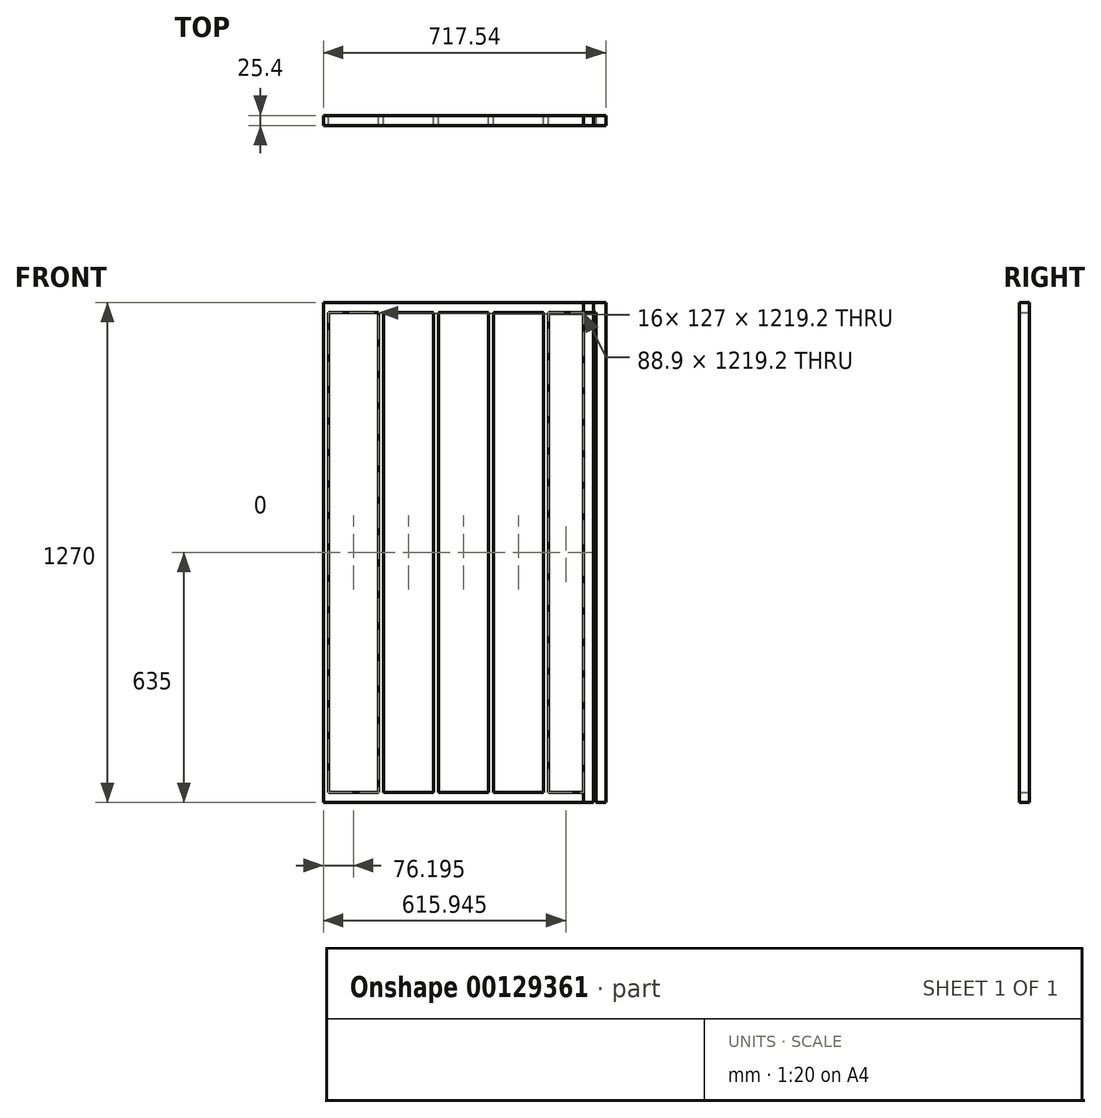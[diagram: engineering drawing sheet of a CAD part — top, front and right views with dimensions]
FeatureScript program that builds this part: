
annotation { "Feature Type Name" : "Feature", "Feature Type Description" : "" }
export const myFeature = defineFeature(function(context is Context, id is Id, definition is map)
    precondition{}
    {
        {
            var Q0;
            Q0=qCreatedBy(makeId("Front.planeOp"),FACE);
            var sketch = newSketch(context, id + "F0", { "sketchPlane" : qUnion([Q0])});
            skLineSegment(sketch, "E0", {"start": v(-930.27, 1244.6) * mm, "end": v(930.27, 1244.6) * mm});
            skLineSegment(sketch, "E1", {"start": v(-930.27, 25.4) * mm, "end": v(930.27, 25.4) * mm});
            skLineSegment(sketch, "E2", {"start": v(-625.48, 25.4) * mm, "end": v(-625.48, 1244.6) * mm, "construction": true});
            skLineSegment(sketch, "E3", {"start": v(-485.77, 1244.6) * mm, "end": v(-485.77, 25.4) * mm, "construction": true});
            skLineSegment(sketch, "E4", {"start": v(-346.08, 25.4) * mm, "end": v(-346.08, 1244.6) * mm, "construction": true});
            skLineSegment(sketch, "E5", {"start": v(-206.37, 1244.6) * mm, "end": v(-206.37, 25.4) * mm, "construction": true});
            skLineSegment(sketch, "E6", {"start": v(-66.67, 25.4) * mm, "end": v(-66.67, 1244.6) * mm, "construction": true});
            skLineSegment(sketch, "E7", {"start": v(73.03, 1244.6) * mm, "end": v(73.03, 25.4) * mm, "construction": true});
            skLineSegment(sketch, "E8", {"start": v(212.73, 25.4) * mm, "end": v(212.73, 1244.6) * mm, "construction": true});
            skLineSegment(sketch, "E9", {"start": v(352.43, 1244.6) * mm, "end": v(352.43, 25.4) * mm, "construction": true});
            skLineSegment(sketch, "E10", {"start": v(492.13, 25.4) * mm, "end": v(492.13, 1244.6) * mm, "construction": true});
            skLineSegment(sketch, "E11", {"start": v(631.82, 1244.6) * mm, "end": v(631.82, 25.4) * mm, "construction": true});
            skLineSegment(sketch, "E12.0", {"start": v(-619.12, 25.4) * mm, "end": v(-619.12, 1244.6) * mm});
            skLineSegment(sketch, "E13.0", {"start": v(-492.12, 1244.6) * mm, "end": v(-492.12, 25.4) * mm});
            skLineSegment(sketch, "E14.0", {"start": v(-479.42, 1244.6) * mm, "end": v(-479.42, 25.4) * mm});
            skLineSegment(sketch, "E15.0", {"start": v(-339.73, 25.4) * mm, "end": v(-339.73, 1244.6) * mm});
            skLineSegment(sketch, "E16.0", {"start": v(-352.43, 25.4) * mm, "end": v(-352.43, 1244.6) * mm});
            skLineSegment(sketch, "E17.0", {"start": v(-212.72, 1244.6) * mm, "end": v(-212.72, 25.4) * mm});
            skLineSegment(sketch, "E18.0", {"start": v(-200.02, 1244.6) * mm, "end": v(-200.02, 25.4) * mm});
            skLineSegment(sketch, "E19.0", {"start": v(-60.32, 25.4) * mm, "end": v(-60.32, 1244.6) * mm});
            skLineSegment(sketch, "E20.0", {"start": v(-73.02, 25.4) * mm, "end": v(-73.02, 1244.6) * mm});
            skLineSegment(sketch, "E21.0", {"start": v(66.68, 1244.6) * mm, "end": v(66.68, 25.4) * mm});
            skLineSegment(sketch, "E22.0", {"start": v(79.38, 1244.6) * mm, "end": v(79.38, 25.4) * mm});
            skLineSegment(sketch, "E23.0", {"start": v(219.08, 25.4) * mm, "end": v(219.08, 1244.6) * mm});
            skLineSegment(sketch, "E24.0", {"start": v(206.38, 25.4) * mm, "end": v(206.38, 1244.6) * mm});
            skLineSegment(sketch, "E25.0", {"start": v(346.08, 1244.6) * mm, "end": v(346.08, 25.4) * mm});
            skLineSegment(sketch, "E26.0", {"start": v(358.78, 1244.6) * mm, "end": v(358.78, 25.4) * mm});
            skLineSegment(sketch, "E27.0", {"start": v(498.48, 25.4) * mm, "end": v(498.48, 1244.6) * mm});
            skLineSegment(sketch, "E28.0", {"start": v(485.78, 25.4) * mm, "end": v(485.78, 1244.6) * mm});
            skLineSegment(sketch, "E29.0", {"start": v(625.48, 1244.6) * mm, "end": v(625.48, 25.4) * mm});
            skLineSegment(sketch, "E30.0", {"start": v(638.18, 1244.6) * mm, "end": v(638.18, 25.4) * mm});
            skLineSegment(sketch, "E31.0", {"start": v(-631.82, 25.4) * mm, "end": v(-631.82, 1244.6) * mm});
            skLineSegment(sketch, "E32.0", {"start": v(-930.27, 1270) * mm, "end": v(930.27, 1270) * mm});
            skLineSegment(sketch, "E33.0", {"start": v(-930.27, 0) * mm, "end": v(930.27, 0) * mm});
            skLineSegment(sketch, "E34", {"start": v(-765.17, 1244.6) * mm, "end": v(-765.17, 25.4) * mm, "construction": true});
            skLineSegment(sketch, "E35", {"start": v(771.52, 25.4) * mm, "end": v(771.52, 1244.6) * mm, "construction": true});
            skLineSegment(sketch, "E36.0", {"start": v(777.88, 25.4) * mm, "end": v(777.88, 1244.6) * mm});
            skLineSegment(sketch, "E37.0", {"start": v(765.18, 25.4) * mm, "end": v(765.18, 1244.6) * mm});
            skLineSegment(sketch, "E38.0", {"start": v(-771.52, 1244.6) * mm, "end": v(-771.52, 25.4) * mm});
            skLineSegment(sketch, "E39.0", {"start": v(-758.82, 1244.6) * mm, "end": v(-758.82, 25.4) * mm});
            skLineSegment(sketch, "E40", {"start": v(930.28, 25.4) * mm, "end": v(930.28, 0) * mm});
            skLineSegment(sketch, "E41", {"start": v(-930.27, 25.4) * mm, "end": v(-930.27, 0) * mm});
            skLineSegment(sketch, "E42", {"start": v(-930.27, 1270) * mm, "end": v(-930.27, 1244.6) * mm});
            skLineSegment(sketch, "E43", {"start": v(930.28, 1270) * mm, "end": v(930.28, 1244.6) * mm});
            skLineSegment(sketch, "E44", {"start": v(-190.5, 1258.47) * mm, "end": v(190.5, 1258.47) * mm});
            skLineSegment(sketch, "E45", {"start": v(0, 1258.47) * mm, "end": v(0, 1270) * mm, "construction": true});
            skLineSegment(sketch, "E46", {"start": v(-190.5, 1258.47) * mm, "end": v(-930.27, 1258.47) * mm, "construction": true});
            skLineSegment(sketch, "E47", {"start": v(190.5, 1258.47) * mm, "end": v(930.27, 1258.47) * mm, "construction": true});
            skLineSegment(sketch, "E48", {"start": v(930.28, 1258.47) * mm, "end": v(930.28, 1270) * mm, "construction": true});
            skLineSegment(sketch, "E49", {"start": v(-930.27, 1258.47) * mm, "end": v(-930.27, 1270) * mm, "construction": true});
            skLineSegment(sketch, "E50", {"start": v(-854.07, 25.4) * mm, "end": v(-854.07, 1244.6) * mm, "construction": true});
            skLineSegment(sketch, "E51", {"start": v(860.42, 25.4) * mm, "end": v(860.43, 1244.6) * mm, "construction": true});
            skLineSegment(sketch, "E52", {"start": v(-854.07, 25.4) * mm, "end": v(-854.07, -210.06) * mm, "construction": true});
            skLineSegment(sketch, "E53", {"start": v(-854.07, -210.06) * mm, "end": v(860.42, -210.06) * mm, "construction": true});
            skLineSegment(sketch, "E54", {"start": v(860.42, -210.06) * mm, "end": v(860.42, 25.4) * mm, "construction": true});
            skSolve(sketch);
        }
        {
            var Q0;
            Q0 = qSketchRegion(id + "F0", true);
            var Q1;
            {var subQ0=sQuery(id+"F0.wireOp",EDGE,"E12.0");Q1=makeQuery(id+"F0.imprint","IMPRINT",FACE,{"disambiguationData":[TD([[makeQuery(id+"F0.imprint","IMPRINT",EDGE,{"derivedFrom":subQ0}),1.0]])]});}
            var Q2;
            {var subQ0=sQuery(id+"F0.wireOp",EDGE,"E13.0");Q2=makeQuery(id+"F0.imprint","IMPRINT",FACE,{"disambiguationData":[TD([[makeQuery(id+"F0.imprint","IMPRINT",EDGE,{"derivedFrom":subQ0}),1.0]])]});}
            var Q3;
            {var subQ0=sQuery(id+"F0.wireOp",EDGE,"E15.0");Q3=makeQuery(id+"F0.imprint","IMPRINT",FACE,{"disambiguationData":[TD([[makeQuery(id+"F0.imprint","IMPRINT",EDGE,{"derivedFrom":subQ0}),1.0]])]});}
            var Q4;
            {var subQ0=sQuery(id+"F0.wireOp",EDGE,"E17.0");Q4=makeQuery(id+"F0.imprint","IMPRINT",FACE,{"disambiguationData":[TD([[makeQuery(id+"F0.imprint","IMPRINT",EDGE,{"derivedFrom":subQ0}),1.0]])]});}
            var Q5;
            {var subQ0=sQuery(id+"F0.wireOp",EDGE,"E19.0");Q5=makeQuery(id+"F0.imprint","IMPRINT",FACE,{"disambiguationData":[TD([[makeQuery(id+"F0.imprint","IMPRINT",EDGE,{"derivedFrom":subQ0}),1.0]])]});}
            var Q6;
            {var subQ0=sQuery(id+"F0.wireOp",EDGE,"E21.0");Q6=makeQuery(id+"F0.imprint","IMPRINT",FACE,{"disambiguationData":[TD([[makeQuery(id+"F0.imprint","IMPRINT",EDGE,{"derivedFrom":subQ0}),1.0]])]});}
            var Q7;
            {var subQ0=sQuery(id+"F0.wireOp",EDGE,"E23.0");Q7=makeQuery(id+"F0.imprint","IMPRINT",FACE,{"disambiguationData":[TD([[makeQuery(id+"F0.imprint","IMPRINT",EDGE,{"derivedFrom":subQ0}),1.0]])]});}
            var Q8;
            {var subQ0=sQuery(id+"F0.wireOp",EDGE,"E25.0");Q8=makeQuery(id+"F0.imprint","IMPRINT",FACE,{"disambiguationData":[TD([[makeQuery(id+"F0.imprint","IMPRINT",EDGE,{"derivedFrom":subQ0}),1.0]])]});}
            var Q9;
            {var subQ0=sQuery(id+"F0.wireOp",EDGE,"E27.0");Q9=makeQuery(id+"F0.imprint","IMPRINT",FACE,{"disambiguationData":[TD([[makeQuery(id+"F0.imprint","IMPRINT",EDGE,{"derivedFrom":subQ0}),1.0]])]});}
            var Q10;
            {var subQ0=sQuery(id+"F0.wireOp",EDGE,"E29.0");Q10=makeQuery(id+"F0.imprint","IMPRINT",FACE,{"disambiguationData":[TD([[makeQuery(id+"F0.imprint","IMPRINT",EDGE,{"derivedFrom":subQ0}),1.0]])]});}
            extrude(context, id + "F1", {"entities" : qUnion([Q0, Q1, Q2, Q3, Q4, Q5, Q6, Q7, Q8, Q9, Q10]), "depth" : 25.4 * mm});
        }
        {
            var Q0;
            Q0=makeQuery(id+"F1.opExtrude","CAP_FACE",FACE,{"disambiguationData":[OSD([sQuery(id+"F0.wireOp",EDGE,"E0"),sQuery(id+"F0.wireOp",EDGE,"E1"),sQuery(id+"F0.wireOp",EDGE,"E12.0"),sQuery(id+"F0.wireOp",EDGE,"E13.0"),sQuery(id+"F0.wireOp",EDGE,"E14.0"),sQuery(id+"F0.wireOp",EDGE,"E15.0"),sQuery(id+"F0.wireOp",EDGE,"E16.0"),sQuery(id+"F0.wireOp",EDGE,"E17.0"),sQuery(id+"F0.wireOp",EDGE,"E18.0"),sQuery(id+"F0.wireOp",EDGE,"E19.0"),sQuery(id+"F0.wireOp",EDGE,"E20.0"),sQuery(id+"F0.wireOp",EDGE,"E21.0"),sQuery(id+"F0.wireOp",EDGE,"E22.0"),sQuery(id+"F0.wireOp",EDGE,"E23.0"),sQuery(id+"F0.wireOp",EDGE,"E24.0"),sQuery(id+"F0.wireOp",EDGE,"E25.0"),sQuery(id+"F0.wireOp",EDGE,"E26.0"),sQuery(id+"F0.wireOp",EDGE,"E27.0"),sQuery(id+"F0.wireOp",EDGE,"E28.0"),sQuery(id+"F0.wireOp",EDGE,"E29.0"),sQuery(id+"F0.wireOp",EDGE,"E30.0"),sQuery(id+"F0.wireOp",EDGE,"E31.0"),sQuery(id+"F0.wireOp",EDGE,"E32.0"),sQuery(id+"F0.wireOp",EDGE,"E33.0"),sQuery(id+"F0.wireOp",EDGE,"E36.0"),sQuery(id+"F0.wireOp",EDGE,"E37.0"),sQuery(id+"F0.wireOp",EDGE,"E38.0"),sQuery(id+"F0.wireOp",EDGE,"E39.0"),sQuery(id+"F0.wireOp",EDGE,"E40"),sQuery(id+"F0.wireOp",EDGE,"E41"),sQuery(id+"F0.wireOp",EDGE,"E42"),sQuery(id+"F0.wireOp",EDGE,"E43")])],"isStart":false});
            var sketch = newSketch(context, id + "F2", { "sketchPlane" : qUnion([Q0])});
            skLineSegment(sketch, "E55.bottom", {"start": v(-200.03, 1292.02) * mm, "end": v(206.37, 1292.02) * mm});
            skLineSegment(sketch, "E55.top", {"start": v(-200.02, -104.94) * mm, "end": v(206.38, -104.94) * mm});
            skLineSegment(sketch, "E55.left", {"start": v(-200.03, 1292.02) * mm, "end": v(-200.02, -104.94) * mm});
            skLineSegment(sketch, "E55.right", {"start": v(206.37, 1292.02) * mm, "end": v(206.38, -104.94) * mm});
            skLineSegment(sketch, "E56.bottom", {"start": v(-930.27, 1270) * mm, "end": v(-860.42, 1270) * mm});
            skLineSegment(sketch, "E56.top", {"start": v(-930.27, 0) * mm, "end": v(-860.42, 0) * mm});
            skLineSegment(sketch, "E56.left", {"start": v(-930.27, 1270) * mm, "end": v(-930.27, 0) * mm});
            skLineSegment(sketch, "E56.right", {"start": v(-860.42, 1270) * mm, "end": v(-860.42, 0) * mm});
            skLineSegment(sketch, "E57.bottom", {"start": v(930.28, 1270) * mm, "end": v(866.77, 1270) * mm});
            skLineSegment(sketch, "E57.top", {"start": v(930.28, 0) * mm, "end": v(866.78, 0) * mm});
            skLineSegment(sketch, "E57.left", {"start": v(930.27, 1270) * mm, "end": v(930.28, 0) * mm});
            skLineSegment(sketch, "E57.right", {"start": v(866.77, 1270) * mm, "end": v(866.78, 0) * mm});
            skSolve(sketch);
        }
        {
            var Q0;
            Q0 = qSketchRegion(id + "F2", true);
            extrude(context, id + "F3", {"entities" : qUnion([Q0]), "operationType" : NewBodyOperationType.REMOVE, "oppositeDirection" : true, "depth" : 25.4 * mm});
        }
        {
            var Q0;
            {var subQ0=sQuery(id+"F0.wireOp",EDGE,"E38.0");var subQ1=sQuery(id+"F0.wireOp",EDGE,"E14.0");var subQ2=sQuery(id+"F0.wireOp",EDGE,"E0");var subQ3=sQuery(id+"F0.wireOp",EDGE,"E16.0");var subQ4=sQuery(id+"F0.wireOp",EDGE,"E32.0");var subQ5=sQuery(id+"F0.wireOp",EDGE,"E31.0");var subQ6=sQuery(id+"F0.wireOp",EDGE,"E13.0");var subQ7=sQuery(id+"F0.wireOp",EDGE,"E33.0");var subQ8=sQuery(id+"F0.wireOp",EDGE,"E42");var subQ9=sQuery(id+"F0.wireOp",EDGE,"E18.0");var subQ10=sQuery(id+"F0.wireOp",EDGE,"E15.0");var subQ11=sQuery(id+"F0.wireOp",EDGE,"E39.0");var subQ12=sQuery(id+"F0.wireOp",EDGE,"E12.0");var subQ13=sQuery(id+"F0.wireOp",EDGE,"E1");var subQ14=sQuery(id+"F0.wireOp",EDGE,"E17.0");var subQ15=sQuery(id+"F0.wireOp",EDGE,"E41");Q0=makeQuery(id+"F3.boolean.opBoolean","SPLIT",FACE,{"disambiguationData":[TD([makeQuery(id+"F1.opExtrude","SWEPT_FACE",FACE,{"disambiguationData":[OSD([subQ12])]})])],"derivedFrom":makeQuery(id+"F1.opExtrude","CAP_FACE",FACE,{"disambiguationData":[OSD([subQ2,subQ13,subQ12,subQ6,subQ1,subQ10,subQ3,subQ14,subQ9,sQuery(id+"F0.wireOp",EDGE,"E19.0"),sQuery(id+"F0.wireOp",EDGE,"E20.0"),sQuery(id+"F0.wireOp",EDGE,"E21.0"),sQuery(id+"F0.wireOp",EDGE,"E22.0"),sQuery(id+"F0.wireOp",EDGE,"E23.0"),sQuery(id+"F0.wireOp",EDGE,"E24.0"),sQuery(id+"F0.wireOp",EDGE,"E25.0"),sQuery(id+"F0.wireOp",EDGE,"E26.0"),sQuery(id+"F0.wireOp",EDGE,"E27.0"),sQuery(id+"F0.wireOp",EDGE,"E28.0"),sQuery(id+"F0.wireOp",EDGE,"E29.0"),sQuery(id+"F0.wireOp",EDGE,"E30.0"),subQ5,subQ4,subQ7,sQuery(id+"F0.wireOp",EDGE,"E36.0"),sQuery(id+"F0.wireOp",EDGE,"E37.0"),subQ0,subQ11,sQuery(id+"F0.wireOp",EDGE,"E40"),subQ15,subQ8,sQuery(id+"F0.wireOp",EDGE,"E43")])],"isStart":false})});}
            var sketch = newSketch(context, id + "F4", { "sketchPlane" : qUnion([Q0])});
            skLineSegment(sketch, "E58", {"start": v(-860.42, 1270) * mm, "end": v(-200.02, 1270) * mm, "construction": true});
            skLineSegment(sketch, "E59", {"start": v(777.88, 1244.6) * mm, "end": v(866.77, 1244.6) * mm, "construction": true});
            skLineSegment(sketch, "E60", {"start": v(206.38, 1270) * mm, "end": v(866.77, 1270) * mm, "construction": true});
            skLineSegment(sketch, "E61", {"start": v(-860.42, 1244.6) * mm, "end": v(-771.52, 1244.6) * mm, "construction": true});
            skLineSegment(sketch, "E62.bottom", {"start": v(-885.82, 1270) * mm, "end": v(-860.42, 1270) * mm});
            skLineSegment(sketch, "E62.top", {"start": v(-885.82, 0) * mm, "end": v(-860.42, 0) * mm});
            skLineSegment(sketch, "E62.left", {"start": v(-885.82, 1270) * mm, "end": v(-885.82, 0) * mm});
            skLineSegment(sketch, "E62.right", {"start": v(-860.42, 1270) * mm, "end": v(-860.42, 0) * mm});
            skLineSegment(sketch, "E63.bottom", {"start": v(866.77, 1270) * mm, "end": v(892.17, 1270) * mm});
            skLineSegment(sketch, "E63.top", {"start": v(866.77, 0) * mm, "end": v(892.17, 0) * mm});
            skLineSegment(sketch, "E63.left", {"start": v(866.77, 1270) * mm, "end": v(866.77, 0) * mm});
            skLineSegment(sketch, "E63.right", {"start": v(892.17, 1270) * mm, "end": v(892.17, 0) * mm});
            skSolve(sketch);
        }
        {
            var Q0;
            Q0 = qSketchRegion(id + "F4", true);
            extrude(context, id + "F5", {"entities" : qUnion([Q0]), "oppositeDirection" : true, "depth" : 25.4 * mm});
        }
        {
            var Q0;
            {var subQ0=sQuery(id+"F0.wireOp",EDGE,"E38.0");var subQ1=sQuery(id+"F0.wireOp",EDGE,"E14.0");var subQ2=sQuery(id+"F0.wireOp",EDGE,"E0");var subQ3=sQuery(id+"F0.wireOp",EDGE,"E16.0");var subQ4=sQuery(id+"F0.wireOp",EDGE,"E32.0");var subQ5=sQuery(id+"F0.wireOp",EDGE,"E31.0");var subQ6=sQuery(id+"F0.wireOp",EDGE,"E13.0");var subQ7=sQuery(id+"F0.wireOp",EDGE,"E33.0");var subQ8=sQuery(id+"F0.wireOp",EDGE,"E42");var subQ9=sQuery(id+"F0.wireOp",EDGE,"E18.0");var subQ10=sQuery(id+"F0.wireOp",EDGE,"E15.0");var subQ11=sQuery(id+"F0.wireOp",EDGE,"E39.0");var subQ12=sQuery(id+"F0.wireOp",EDGE,"E12.0");var subQ13=sQuery(id+"F0.wireOp",EDGE,"E1");var subQ14=sQuery(id+"F0.wireOp",EDGE,"E17.0");var subQ15=sQuery(id+"F0.wireOp",EDGE,"E41");Q0=makeQuery(id+"F3.boolean.opBoolean","SPLIT",FACE,{"disambiguationData":[TD([makeQuery(id+"F1.opExtrude","SWEPT_FACE",FACE,{"disambiguationData":[OSD([subQ12])]})])],"derivedFrom":makeQuery(id+"F1.opExtrude","CAP_FACE",FACE,{"disambiguationData":[OSD([subQ2,subQ13,subQ12,subQ6,subQ1,subQ10,subQ3,subQ14,subQ9,sQuery(id+"F0.wireOp",EDGE,"E19.0"),sQuery(id+"F0.wireOp",EDGE,"E20.0"),sQuery(id+"F0.wireOp",EDGE,"E21.0"),sQuery(id+"F0.wireOp",EDGE,"E22.0"),sQuery(id+"F0.wireOp",EDGE,"E23.0"),sQuery(id+"F0.wireOp",EDGE,"E24.0"),sQuery(id+"F0.wireOp",EDGE,"E25.0"),sQuery(id+"F0.wireOp",EDGE,"E26.0"),sQuery(id+"F0.wireOp",EDGE,"E27.0"),sQuery(id+"F0.wireOp",EDGE,"E28.0"),sQuery(id+"F0.wireOp",EDGE,"E29.0"),sQuery(id+"F0.wireOp",EDGE,"E30.0"),subQ5,subQ4,subQ7,sQuery(id+"F0.wireOp",EDGE,"E36.0"),sQuery(id+"F0.wireOp",EDGE,"E37.0"),subQ0,subQ11,sQuery(id+"F0.wireOp",EDGE,"E40"),subQ15,subQ8,sQuery(id+"F0.wireOp",EDGE,"E43")])],"isStart":false})});}
            var sketch = newSketch(context, id + "F6", { "sketchPlane" : qUnion([Q0])});
            skLineSegment(sketch, "E64.bottom", {"start": v(-917.57, 1270) * mm, "end": v(-892.17, 1270) * mm});
            skLineSegment(sketch, "E64.top", {"start": v(-917.57, 0) * mm, "end": v(-892.17, 0) * mm});
            skLineSegment(sketch, "E64.left", {"start": v(-917.57, 1270) * mm, "end": v(-917.57, 0) * mm});
            skLineSegment(sketch, "E64.right", {"start": v(-892.17, 1270) * mm, "end": v(-892.17, 0) * mm});
            skLineSegment(sketch, "E65.bottom", {"start": v(898.52, 1270) * mm, "end": v(923.92, 1270) * mm});
            skLineSegment(sketch, "E65.top", {"start": v(898.52, 0) * mm, "end": v(923.92, 0) * mm});
            skLineSegment(sketch, "E65.left", {"start": v(898.52, 1270) * mm, "end": v(898.52, 0) * mm});
            skLineSegment(sketch, "E65.right", {"start": v(923.92, 1270) * mm, "end": v(923.92, 0) * mm});
            skLineSegment(sketch, "E66", {"start": v(-892.17, 1270) * mm, "end": v(-885.82, 1270) * mm, "construction": true});
            skLineSegment(sketch, "E67", {"start": v(898.52, 1270) * mm, "end": v(892.17, 1270) * mm, "construction": true});
            skLineSegment(sketch, "E68.bottom", {"start": v(923.92, 1270) * mm, "end": v(866.77, 1270) * mm});
            skLineSegment(sketch, "E68.top", {"start": v(923.92, 1244.6) * mm, "end": v(866.77, 1244.6) * mm});
            skLineSegment(sketch, "E68.left", {"start": v(923.92, 1270) * mm, "end": v(923.92, 1244.6) * mm});
            skLineSegment(sketch, "E68.right", {"start": v(866.77, 1270) * mm, "end": v(866.77, 1244.6) * mm});
            skSolve(sketch);
        }
        {
            var Q0;
            Q0 = qSketchRegion(id + "F6", true);
            extrude(context, id + "F7", {"entities" : qUnion([Q0]), "oppositeDirection" : true, "depth" : 25.4 * mm});
        }
        {
            var Q0;
            Q0=makeQuery(id+"F5.opExtrude","SWEPT_BODY",BODY,{"disambiguationData":[OSD([sQuery(id+"F4.wireOp",EDGE,"E63.bottom"),sQuery(id+"F4.wireOp",EDGE,"E63.top"),sQuery(id+"F4.wireOp",EDGE,"E63.left"),sQuery(id+"F4.wireOp",EDGE,"E63.right")])]});
            var Q1;
            Q1=makeQuery(id+"F3.boolean.opBoolean","SPLIT",BODY,{"disambiguationData":[OD(1.0)],"derivedFrom":makeQuery(id+"F1.opExtrude","SWEPT_BODY",BODY,{"disambiguationData":[OSD([sQuery(id+"F0.wireOp",EDGE,"E0"),sQuery(id+"F0.wireOp",EDGE,"E1"),sQuery(id+"F0.wireOp",EDGE,"E12.0"),sQuery(id+"F0.wireOp",EDGE,"E13.0"),sQuery(id+"F0.wireOp",EDGE,"E14.0"),sQuery(id+"F0.wireOp",EDGE,"E15.0"),sQuery(id+"F0.wireOp",EDGE,"E16.0"),sQuery(id+"F0.wireOp",EDGE,"E17.0"),sQuery(id+"F0.wireOp",EDGE,"E18.0"),sQuery(id+"F0.wireOp",EDGE,"E19.0"),sQuery(id+"F0.wireOp",EDGE,"E20.0"),sQuery(id+"F0.wireOp",EDGE,"E21.0"),sQuery(id+"F0.wireOp",EDGE,"E22.0"),sQuery(id+"F0.wireOp",EDGE,"E23.0"),sQuery(id+"F0.wireOp",EDGE,"E24.0"),sQuery(id+"F0.wireOp",EDGE,"E25.0"),sQuery(id+"F0.wireOp",EDGE,"E26.0"),sQuery(id+"F0.wireOp",EDGE,"E27.0"),sQuery(id+"F0.wireOp",EDGE,"E28.0"),sQuery(id+"F0.wireOp",EDGE,"E29.0"),sQuery(id+"F0.wireOp",EDGE,"E30.0"),sQuery(id+"F0.wireOp",EDGE,"E31.0"),sQuery(id+"F0.wireOp",EDGE,"E32.0"),sQuery(id+"F0.wireOp",EDGE,"E33.0"),sQuery(id+"F0.wireOp",EDGE,"E36.0"),sQuery(id+"F0.wireOp",EDGE,"E37.0"),sQuery(id+"F0.wireOp",EDGE,"E38.0"),sQuery(id+"F0.wireOp",EDGE,"E39.0"),sQuery(id+"F0.wireOp",EDGE,"E40"),sQuery(id+"F0.wireOp",EDGE,"E41"),sQuery(id+"F0.wireOp",EDGE,"E42"),sQuery(id+"F0.wireOp",EDGE,"E43")])]})});
            booleanBodies(context, id + "F8", {"operationType" : BooleanOperationType.UNION, "tools" : qUnion([Q0, Q1])});
        }
        {
            var Q0;
            Q0=makeQuery(id+"F7.opExtrude","CAP_FACE",FACE,{"disambiguationData":[OSD([sQuery(id+"F6.wireOp",EDGE,"E65.top"),sQuery(id+"F6.wireOp",EDGE,"E65.left"),sQuery(id+"F6.wireOp",EDGE,"E65.right"),sQuery(id+"F6.wireOp",EDGE,"E68.bottom"),sQuery(id+"F6.wireOp",EDGE,"E68.top"),sQuery(id+"F6.wireOp",EDGE,"E68.left"),sQuery(id+"F6.wireOp",EDGE,"E68.right")])],"isStart":false});
            var sketch = newSketch(context, id + "F9", { "sketchPlane" : qUnion([Q0])});
            skLineSegment(sketch, "E69", {"start": v(-962.02, 0) * mm, "end": v(-923.92, 0) * mm, "construction": true});
            skLineSegment(sketch, "E70", {"start": v(-866.77, 1193.7) * mm, "end": v(860.42, 1193.7) * mm, "construction": true});
            skLineSegment(sketch, "E71", {"start": v(-206.38, 939.29) * mm, "end": v(200.02, 939.29) * mm, "construction": true});
            skLineSegment(sketch, "E72.bottom", {"start": v(178.8, 1313.1) * mm, "end": v(1154.55, 1313.1) * mm});
            skLineSegment(sketch, "E72.top", {"start": v(178.8, -110.67) * mm, "end": v(1154.55, -110.67) * mm});
            skLineSegment(sketch, "E72.left", {"start": v(178.8, 1313.1) * mm, "end": v(178.8, -110.67) * mm});
            skLineSegment(sketch, "E72.right", {"start": v(1154.55, 1313.1) * mm, "end": v(1154.55, -110.67) * mm});
            skSolve(sketch);
        }
        {
            var Q0;
            Q0 = qSketchRegion(id + "F9", true);
            extrude(context, id + "F10", {"entities" : qUnion([Q0]), "operationType" : NewBodyOperationType.REMOVE, "oppositeDirection" : true, "depth" : 218.68 * mm});
        }
    });
